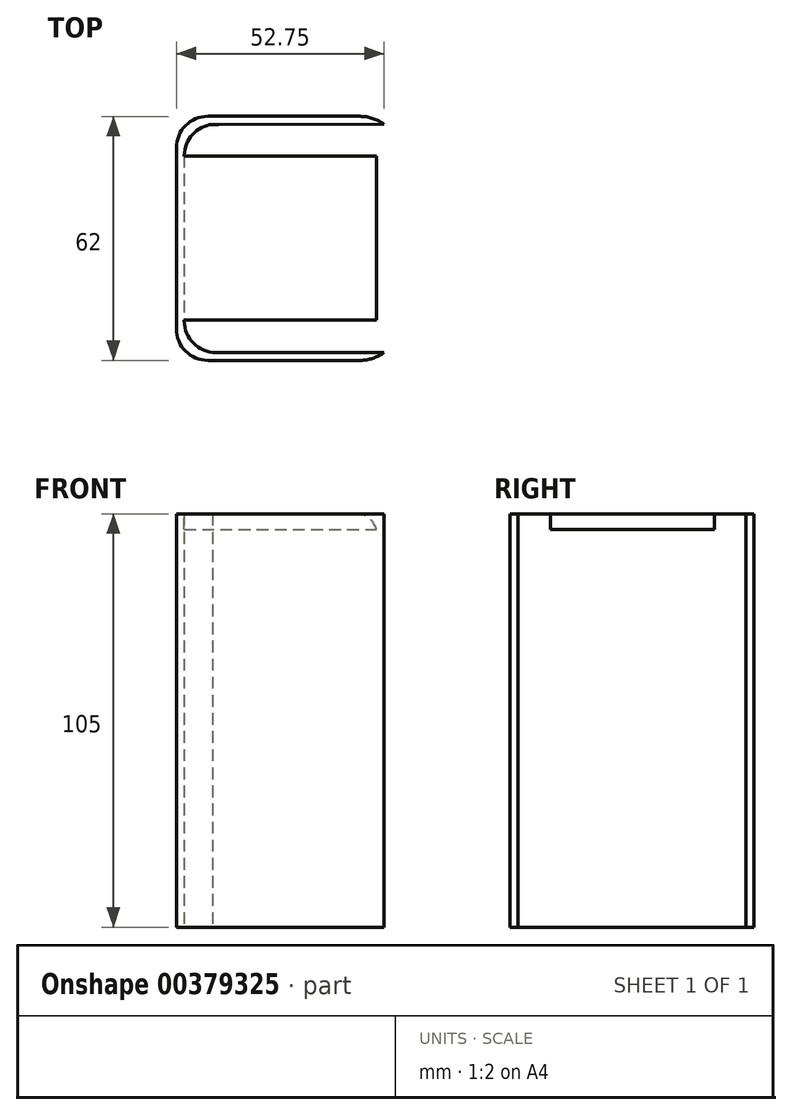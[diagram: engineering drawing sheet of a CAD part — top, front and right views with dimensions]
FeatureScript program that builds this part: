
annotation { "Feature Type Name" : "Feature", "Feature Type Description" : "" }
export const myFeature = defineFeature(function(context is Context, id is Id, definition is map)
    precondition{}
    {
        {
            var Q0;
            Q0=qCreatedBy(makeId("Top.planeOp"),FACE);
            var sketch = newSketch(context, id + "F0", { "sketchPlane" : qUnion([Q0])});
            skLineSegment(sketch, "E0.top", {"start": v(-19.5, -29.52) * mm, "end": v(23.25, -29.52) * mm});
            skLineSegment(sketch, "E0.left", {"start": v(-27.5, 20.48) * mm, "end": v(-27.5, -21.52) * mm});
            skArc(sketch, "E1.filletArc", {"start": v(-27.5, -21.52) * mm, "mid": v(-25.16, -27.17) * mm, "end": v(-19.5, -29.52) * mm});
            skLineSegment(sketch, "E2.top", {"start": v(-21.5, -31.52) * mm, "end": v(-19.5, -31.52) * mm});
            skLineSegment(sketch, "E2.left", {"start": v(-29.5, -21.52) * mm, "end": v(-29.5, -23.52) * mm});
            skArc(sketch, "E3.filletArc", {"start": v(-29.5, -23.52) * mm, "mid": v(-27.16, -29.17) * mm, "end": v(-21.5, -31.52) * mm});
            skArc(sketch, "E4.filletArc", {"start": v(-20.27, 28.45) * mm, "mid": v(-25.42, 25.86) * mm, "end": v(-27.5, 20.48) * mm});
            skLineSegment(sketch, "E5", {"start": v(-13.88, 30.46) * mm, "end": v(-13.88, 30.48) * mm});
            skLineSegment(sketch, "E6", {"start": v(-29.5, -21.52) * mm, "end": v(-29.5, 20.48) * mm});
            skLineSegment(sketch, "E7", {"start": v(-19.5, -31.52) * mm, "end": v(23.25, -31.52) * mm});
            skLineSegment(sketch, "E8", {"start": v(-29.5, 20.48) * mm, "end": v(-29.5, 22.5) * mm});
            skArc(sketch, "E9.filletArc", {"start": v(-21.5, 30.48) * mm, "mid": v(-27.15, 28.15) * mm, "end": v(-29.5, 22.5) * mm});
            skLineSegment(sketch, "E10", {"start": v(-20.27, 28.45) * mm, "end": v(-18.76, 28.45) * mm});
            skLineSegment(sketch, "E11", {"start": v(-18.76, 30.48) * mm, "end": v(-21.5, 30.48) * mm});
            skLineSegment(sketch, "E12.left", {"start": v(-29.5, 20.48) * mm, "end": v(-29.5, -23.52) * mm});
            skLineSegment(sketch, "E13", {"start": v(23.25, -29.52) * mm, "end": v(23.25, -31.52) * mm});
            skLineSegment(sketch, "E14", {"start": v(-18.76, 30.48) * mm, "end": v(23.25, 30.48) * mm});
            skLineSegment(sketch, "E15", {"start": v(23.25, 30.48) * mm, "end": v(23.25, 28.48) * mm});
            skLineSegment(sketch, "E16", {"start": v(23.25, 28.48) * mm, "end": v(-18.76, 28.45) * mm});
            skSolve(sketch);
        }
        {
            var Q0;
            {var subQ0=sQuery(id+"F0.wireOp",EDGE,"E1.filletArc");Q0=makeQuery(id+"F0.imprint","IMPRINT",FACE,{"disambiguationData":[TD([[makeQuery(id+"F0.imprint","IMPRINT",EDGE,{"derivedFrom":subQ0}),1.0]])]});}
            var Q1;
            {var subQ0=sQuery(id+"F0.wireOp",EDGE,"E1.filletArc");Q1=makeQuery(id+"F0.imprint","IMPRINT",FACE,{"disambiguationData":[TD([[makeQuery(id+"F0.imprint","IMPRINT",EDGE,{"derivedFrom":subQ0}),-1.0]])]});}
            extrude(context, id + "F1", {"entities" : qUnion([Q0, Q1]), "depth" : 2 * mm, "offsetDistance" : 25.4 * mm});
        }
        {
            var Q0;
            {var subQ4=sQuery(id+"F0.wireOp",EDGE,"1476cd65-4088-49d8-92c3-a141a03b2ac3.filletArc");Q0=makeQuery(id+"F0.imprint","IMPRINT",FACE,{"disambiguationData":[TD([[makeQuery(id+"F0.imprint","IMPRINT",EDGE,{"derivedFrom":subQ4}),-1.0]])]});}
            var Q1;
            {var subQ0=sQuery(id+"F0.wireOp",EDGE,"E1.filletArc");Q1=makeQuery(id+"F0.imprint","IMPRINT",FACE,{"disambiguationData":[TD([[makeQuery(id+"F0.imprint","IMPRINT",EDGE,{"derivedFrom":subQ0}),-1.0]])]});}
            var Q2;
            {var subQ4=sQuery(id+"F0.wireOp",EDGE,"E4.filletArc");Q2=makeQuery(id+"F0.imprint","IMPRINT",FACE,{"disambiguationData":[TD([[makeQuery(id+"F0.imprint","IMPRINT",EDGE,{"derivedFrom":subQ4}),-1.0]])]});}
            extrude(context, id + "F2", {"entities" : qUnion([Q0, Q1, Q2]), "operationType" : NewBodyOperationType.ADD, "oppositeDirection" : true, "depth" : 103 * mm, "offsetDistance" : 25.4 * mm});
        }
        {
            var Q0;
            Q0=qCreatedBy(makeId("Top.planeOp"),FACE);
            var sketch = newSketch(context, id + "F3", { "sketchPlane" : qUnion([Q0])});
            skLineSegment(sketch, "E17.bottom", {"start": v(-29.5, 20.42) * mm, "end": v(21.3, 20.42) * mm});
            skLineSegment(sketch, "E17.top", {"start": v(-29.5, -21.25) * mm, "end": v(21.3, -21.25) * mm});
            skLineSegment(sketch, "E17.left", {"start": v(-29.5, 20.42) * mm, "end": v(-29.5, -21.25) * mm});
            skLineSegment(sketch, "E18", {"start": v(21.3, 20.42) * mm, "end": v(21.3, -21.25) * mm});
            skSolve(sketch);
        }
        {
            var Q0;
            Q0=makeQuery(id+"F3.imprint","IMPRINT",FACE,{"disambiguationData":[TD([[makeQuery(id+"F3.imprint","IMPRINT",EDGE,{"derivedFrom":sQuery(id+"F3.wireOp",EDGE,"rrh3U2Ua-GgIZ-SF6a-3gdQ-TyNM70nd97vX")}),-1.0]])]});
            var Q1;
            Q1=makeQuery(id+"F3.imprint","IMPRINT",FACE,{"disambiguationData":[TD([[makeQuery(id+"F3.imprint","IMPRINT",EDGE,{"derivedFrom":sQuery(id+"F3.wireOp",EDGE,"E17.bottom")}),-1.0]])]});
            extrude(context, id + "F4", {"entities" : qUnion([Q0, Q1]), "operationType" : NewBodyOperationType.ADD, "endBound" : BoundingType.SYMMETRIC, "depth" : 4 * mm, "offsetDistance" : 25.4 * mm});
        }
        {
            var Q0;
            {var subQ0=sQuery(id+"F0.wireOp",EDGE,"E15");var subQ1=sQuery(id+"F0.wireOp",EDGE,"E14");Q0=makeQuery(id+"F2.boolean.opBoolean","MERGE",EDGE,{"derivedFrom":[makeQuery(id+"F1.opExtrude","SWEPT_EDGE",EDGE,{"disambiguationData":[OSD([subQ1,subQ0])]}),makeQuery(id+"F2.opExtrude","SWEPT_EDGE",EDGE,{"disambiguationData":[OSD([subQ1,subQ0])]})]});}
            var Q1;
            {var subQ0=sQuery(id+"F0.wireOp",EDGE,"E13");var subQ1=sQuery(id+"F0.wireOp",EDGE,"E7");Q1=makeQuery(id+"F2.boolean.opBoolean","MERGE",EDGE,{"derivedFrom":[makeQuery(id+"F1.opExtrude","SWEPT_EDGE",EDGE,{"disambiguationData":[OSD([subQ1,subQ0])]}),makeQuery(id+"F2.opExtrude","SWEPT_EDGE",EDGE,{"disambiguationData":[OSD([subQ1,subQ0])]})]});}
            fillet(context, id + "F5", {"entities" : qUnion([Q0, Q1]), "radius" : 10.16 * mm, "tangentPropagation" : true, "allowEdgeOverflow" : false});
        }
        {
            var Q0;
            Q0=makeQuery(id+"F4.opExtrude","CAP_EDGE",EDGE,{"disambiguationData":[OSD([sQuery(id+"F3.wireOp",EDGE,"E18")])],"isStart":false});
            fillet(context, id + "F6", {"entities" : qUnion([Q0]), "radius" : 5.08 * mm, "tangentPropagation" : true, "allowEdgeOverflow" : false});
        }
    });
